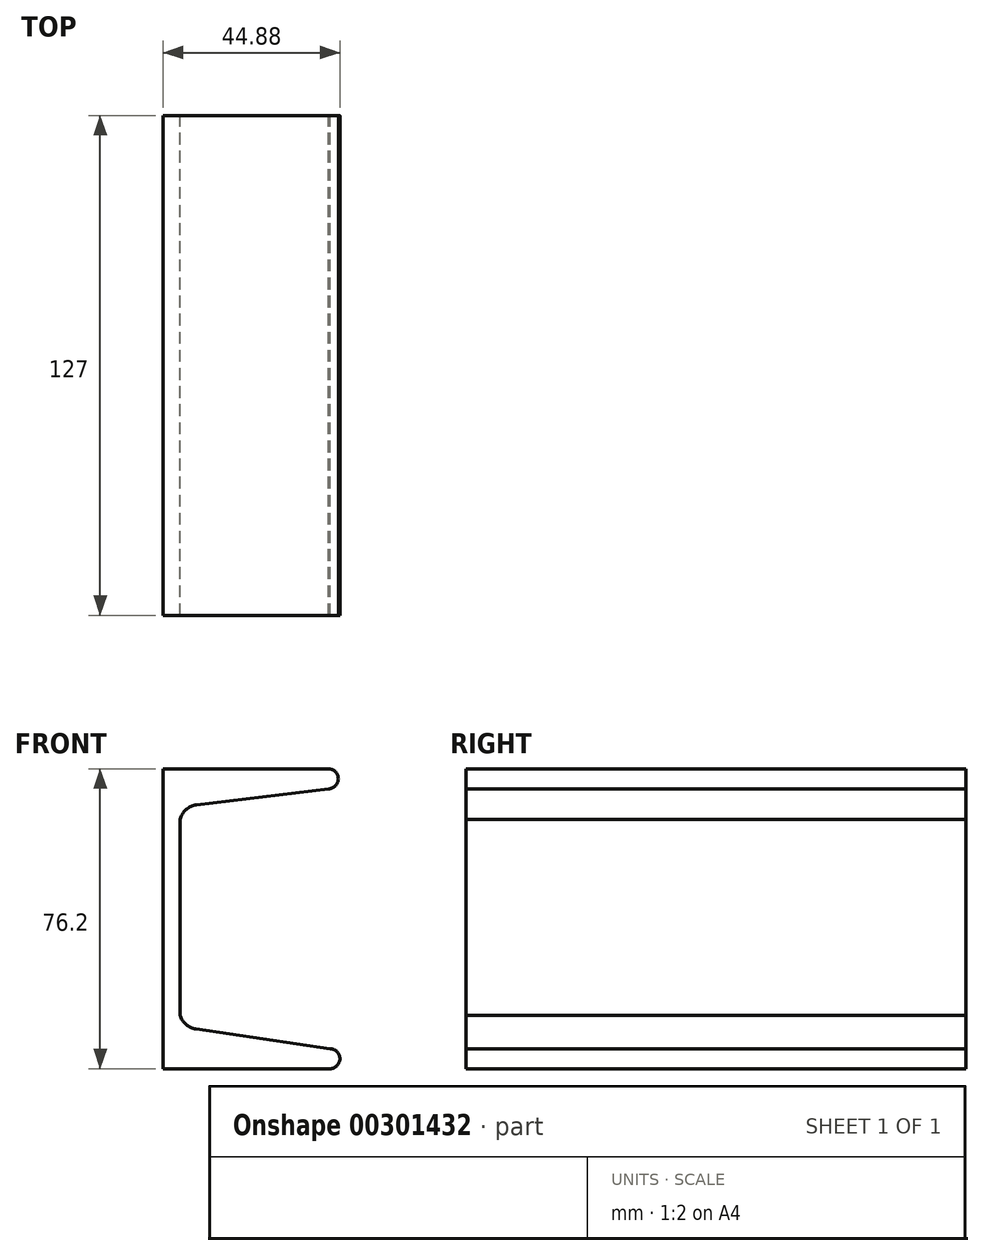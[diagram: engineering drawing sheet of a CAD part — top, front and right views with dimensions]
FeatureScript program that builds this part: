
annotation { "Feature Type Name" : "Feature", "Feature Type Description" : "" }
export const myFeature = defineFeature(function(context is Context, id is Id, definition is map)
    precondition{}
    {
        {
            var Q0;
            Q0=qCreatedBy(makeId("Front.planeOp"),FACE);
            var sketch = newSketch(context, id + "F0", { "sketchPlane" : qUnion([Q0])});
            skLineSegment(sketch, "E0", {"start": v(0, 0) * mm, "end": v(0, 76.2) * mm});
            skLineSegment(sketch, "E1", {"start": v(0, 76.2) * mm, "end": v(41.93, 76.2) * mm});
            skLineSegment(sketch, "E2", {"start": v(0, 0) * mm, "end": v(42.34, 0) * mm});
            skLineSegment(sketch, "E3", {"start": v(4.32, 63.33) * mm, "end": v(4.32, 13.57) * mm});
            skArc(sketch, "E4", {"start": v(42.34, 0) * mm, "mid": v(44.88, 2.54) * mm, "end": v(42.34, 5.08) * mm});
            skArc(sketch, "E5", {"start": v(41.93, 76.2) * mm, "mid": v(44.47, 73.66) * mm, "end": v(41.93, 71.12) * mm});
            skLineSegment(sketch, "E6", {"start": v(41.93, 71.12) * mm, "end": v(8.44, 67.01) * mm});
            skLineSegment(sketch, "E7", {"start": v(42.34, 5.08) * mm, "end": v(8.28, 10.08) * mm});
            skArc(sketch, "E8", {"start": v(8.44, 67.01) * mm, "mid": v(5.8, 65.82) * mm, "end": v(4.32, 63.33) * mm});
            skArc(sketch, "E9", {"start": v(8.28, 10.08) * mm, "mid": v(5.79, 11.24) * mm, "end": v(4.32, 13.57) * mm});
            skSolve(sketch);
        }
        {
            var Q0;
            Q0=makeQuery(id+"F0.imprint","IMPRINT",FACE,{"disambiguationData":[TD([[makeQuery(id+"F0.imprint","IMPRINT",EDGE,{"derivedFrom":sQuery(id+"F0.wireOp",EDGE,"E0")}),-1.0]])]});
            extrude(context, id + "F1", {"entities" : qUnion([Q0]), "depth" : 127 * mm});
        }
    });
